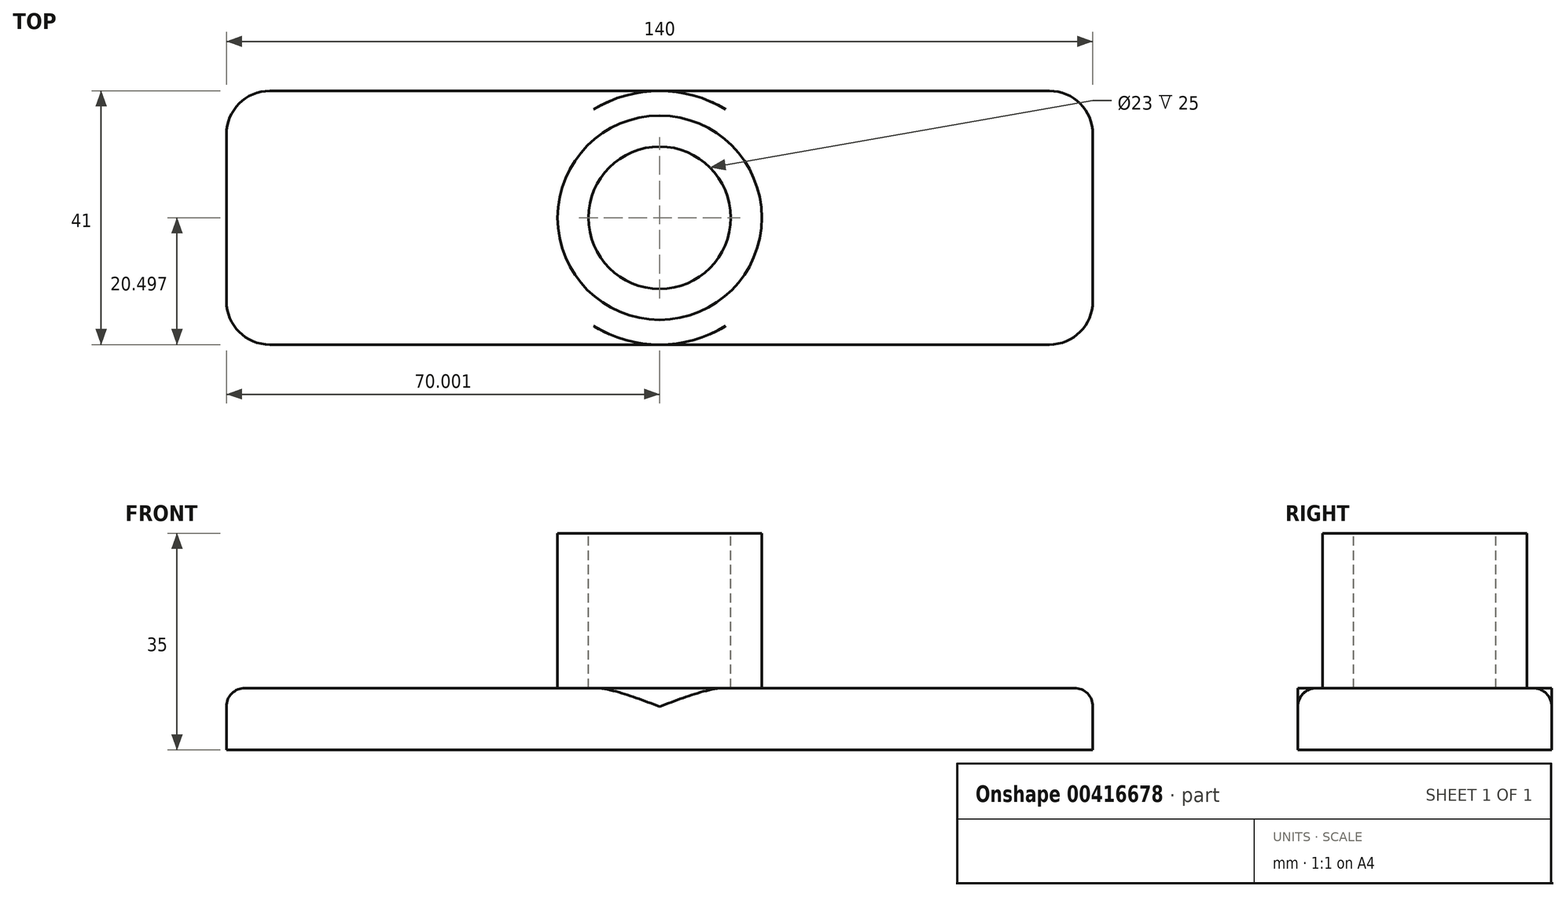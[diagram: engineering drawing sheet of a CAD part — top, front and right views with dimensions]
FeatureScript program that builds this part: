
annotation { "Feature Type Name" : "Feature", "Feature Type Description" : "" }
export const myFeature = defineFeature(function(context is Context, id is Id, definition is map)
    precondition{}
    {
        {
            var Q0;
            Q0=qCreatedBy(makeId("Top.planeOp"),FACE);
            var sketch = newSketch(context, id + "F0", { "sketchPlane" : qUnion([Q0])});
            skLineSegment(sketch, "E0.bottom", {"start": v(-93.82, 2.66) * mm, "end": v(46.18, 2.66) * mm});
            skLineSegment(sketch, "E0.top", {"start": v(-93.82, -38.34) * mm, "end": v(46.18, -38.34) * mm});
            skLineSegment(sketch, "E0.left", {"start": v(-93.82, 2.66) * mm, "end": v(-93.82, -38.34) * mm});
            skLineSegment(sketch, "E0.right", {"start": v(46.18, 2.66) * mm, "end": v(46.18, -38.34) * mm});
            skSolve(sketch);
        }
        {
            var Q0;
            Q0=makeQuery(id+"F0.imprint","IMPRINT",FACE,{"disambiguationData":[TD([[makeQuery(id+"F0.imprint","IMPRINT",EDGE,{"derivedFrom":sQuery(id+"F0.wireOp",EDGE,"E0.bottom")}),-1.0]])]});
            extrude(context, id + "F1", {"entities" : qUnion([Q0]), "depth" : 10 * mm});
        }
        {
            var Q0;
            Q0=makeQuery(id+"F1.opExtrude","CAP_FACE",FACE,{"disambiguationData":[OSD([sQuery(id+"F0.wireOp",EDGE,"E0.bottom"),sQuery(id+"F0.wireOp",EDGE,"E0.top"),sQuery(id+"F0.wireOp",EDGE,"E0.left"),sQuery(id+"F0.wireOp",EDGE,"E0.right")])],"isStart":false});
            var sketch = newSketch(context, id + "F2", { "sketchPlane" : qUnion([Q0])});
            skLineSegment(sketch, "E1", {"start": v(-23.82, 2.66) * mm, "end": v(-23.82, -38.34) * mm, "construction": true});
            skLineSegment(sketch, "E2", {"start": v(-93.82, -17.84) * mm, "end": v(46.18, -17.84) * mm, "construction": true});
            skSolve(sketch);
        }
        {
            var Q0;
            Q0=makeQuery(id+"F2.imprint","IMPRINT",FACE,{"disambiguationData":[TD([[makeQuery(id+"F2.imprint","IMPRINT",EDGE,{"derivedFrom":makeQuery(id+"F1.opExtrude","CAP_EDGE",EDGE,{"disambiguationData":[OSD([sQuery(id+"F0.wireOp",EDGE,"E0.bottom")])],"isStart":false})}),-1.0]])]});
            var sketch = newSketch(context, id + "F3", { "sketchPlane" : qUnion([Q0])});
            skCircle(sketch, "E3", {"center": v(-23.82, -17.84) * mm, "radius": 16.5 * mm});
            skSolve(sketch);
        }
        {
            var Q0;
            Q0=makeQuery(id+"F3.imprint","IMPRINT",FACE,{"disambiguationData":[TD([[makeQuery(id+"F3.imprint","IMPRINT",EDGE,{"derivedFrom":sQuery(id+"F3.wireOp",EDGE,"E3")}),1.0]])]});
            extrude(context, id + "F4", {"entities" : qUnion([Q0]), "operationType" : NewBodyOperationType.ADD, "depth" : 25 * mm});
        }
        {
            var Q0;
            Q0=makeQuery(id+"F4.opExtrude","CAP_FACE",FACE,{"disambiguationData":[OSD([sQuery(id+"F3.wireOp",EDGE,"E3")])],"isStart":false});
            var sketch = newSketch(context, id + "F5", { "sketchPlane" : qUnion([Q0])});
            skCircle(sketch, "E4", {"center": v(-23.82, -17.84) * mm, "radius": 11.5 * mm});
            skSolve(sketch);
        }
        {
            var Q0;
            Q0=makeQuery(id+"F5.imprint","IMPRINT",FACE,{"disambiguationData":[TD([[makeQuery(id+"F5.imprint","IMPRINT",EDGE,{"derivedFrom":sQuery(id+"F5.wireOp",EDGE,"E4")}),1.0]])]});
            extrude(context, id + "F6", {"entities" : qUnion([Q0]), "operationType" : NewBodyOperationType.REMOVE, "oppositeDirection" : true, "depth" : 25 * mm});
        }
        {
            var Q0;
            Q0=makeQuery(id+"F1.opExtrude","CAP_FACE",FACE,{"disambiguationData":[OSD([sQuery(id+"F0.wireOp",EDGE,"E0.bottom"),sQuery(id+"F0.wireOp",EDGE,"E0.top"),sQuery(id+"F0.wireOp",EDGE,"E0.left"),sQuery(id+"F0.wireOp",EDGE,"E0.right")])],"isStart":true});
            var sketch = newSketch(context, id + "F7", { "sketchPlane" : qUnion([Q0])});
            skLineSegment(sketch, "E5.bottom", {"start": v(36.18, 28.34) * mm, "end": v(-83.82, 28.34) * mm});
            skLineSegment(sketch, "E5.top", {"start": v(36.18, 7.34) * mm, "end": v(-83.82, 7.34) * mm});
            skLineSegment(sketch, "E5.left", {"start": v(36.18, 28.34) * mm, "end": v(36.18, 7.34) * mm});
            skLineSegment(sketch, "E5.right", {"start": v(-83.82, 28.34) * mm, "end": v(-83.82, 7.34) * mm});
            skPoint(sketch, "E5.middle", {"position": v(-23.82, 17.84) * mm});
            skPoint(sketch, "E5.middle.positionSnap0", {"position": v(46.18, 17.84) * mm});
            skPoint(sketch, "E5.centerSnap0", {"position": v(46.18, 17.84) * mm});
            skSolve(sketch);
        }
        {
            var Q0;
            Q0=makeQuery(id+"F1.opExtrude","SWEPT_EDGE",EDGE,{"disambiguationData":[OSD([sQuery(id+"F0.wireOp",EDGE,"E0.top"),sQuery(id+"F0.wireOp",EDGE,"E0.left")])]});
            var Q1;
            Q1=makeQuery(id+"F1.opExtrude","SWEPT_EDGE",EDGE,{"disambiguationData":[OSD([sQuery(id+"F0.wireOp",EDGE,"E0.top"),sQuery(id+"F0.wireOp",EDGE,"E0.right")])]});
            var Q2;
            Q2=makeQuery(id+"F1.opExtrude","SWEPT_EDGE",EDGE,{"disambiguationData":[OSD([sQuery(id+"F0.wireOp",EDGE,"E0.bottom"),sQuery(id+"F0.wireOp",EDGE,"E0.right")])]});
            var Q3;
            Q3=makeQuery(id+"F1.opExtrude","SWEPT_EDGE",EDGE,{"disambiguationData":[OSD([sQuery(id+"F0.wireOp",EDGE,"E0.bottom"),sQuery(id+"F0.wireOp",EDGE,"E0.left")])]});
            fillet(context, id + "F8", {"entities" : qUnion([Q0, Q1, Q2, Q3]), "radius" : 7 * mm, "tangentPropagation" : true, "allowEdgeOverflow" : false});
        }
        {
            var Q0;
            Q0=makeQuery(id+"F1.opExtrude","CAP_EDGE",EDGE,{"disambiguationData":[OSD([sQuery(id+"F0.wireOp",EDGE,"E0.top")])],"isStart":false});
            fillet(context, id + "F9", {"entities" : qUnion([Q0]), "radius" : 3 * mm, "tangentPropagation" : true, "allowEdgeOverflow" : false});
        }
        {
            var Q0;
            Q0=makeQuery(id+"F2.imprint","IMPRINT",FACE,{"disambiguationData":[TD([[makeQuery(id+"F2.imprint","IMPRINT",EDGE,{"derivedFrom":makeQuery(id+"F1.opExtrude","CAP_EDGE",EDGE,{"disambiguationData":[OSD([sQuery(id+"F0.wireOp",EDGE,"E0.bottom")])],"isStart":false})}),-1.0]])]});
            var sketch = newSketch(context, id + "F10", { "sketchPlane" : qUnion([Q0])});
            skCircle(sketch, "E6", {"center": v(-23.82, -17.84) * mm, "radius": 20.5 * mm});
            skSolve(sketch);
        }
        {
            var Q0;
            {var subQ0=sQuery(id+"F10.wireOp",EDGE,"E6");var subQ1=makeQuery(id+"F10.imprint","INTERSECT",VERTEX,{"derivedFrom":[makeQuery(id+"F2.imprint","IMPRINT",EDGE,{"derivedFrom":makeQuery(id+"F1.opExtrude","CAP_EDGE",EDGE,{"disambiguationData":[OSD([sQuery(id+"F0.wireOp",EDGE,"E0.bottom")])],"isStart":false})}),subQ0]});Q0=makeQuery(id+"F10.imprint","IMPRINT",FACE,{"disambiguationData":[TD([[makeQuery(id+"F10.imprint","IMPRINT",EDGE,{"disambiguationData":[TD([[subQ1,-1.0]])],"derivedFrom":subQ0}),1.0]])]});}
            extrude(context, id + "F11", {"entities" : qUnion([Q0]), "operationType" : NewBodyOperationType.ADD, "oppositeDirection" : true, "depth" : 5 * mm});
        }
    });
